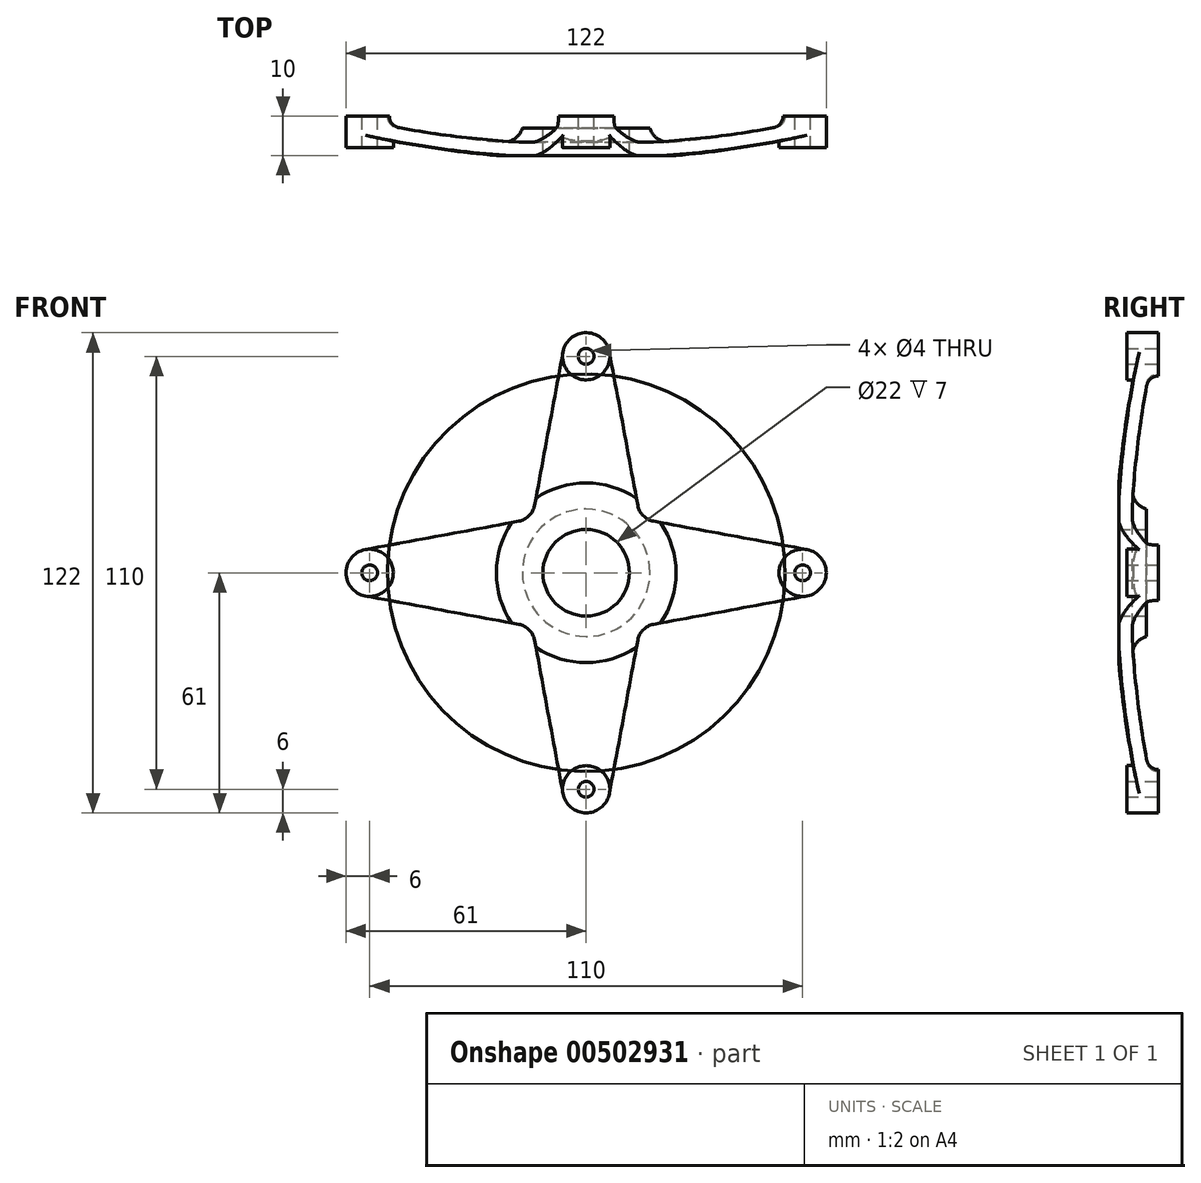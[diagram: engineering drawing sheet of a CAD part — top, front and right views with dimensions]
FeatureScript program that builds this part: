
annotation { "Feature Type Name" : "Feature", "Feature Type Description" : "" }
export const myFeature = defineFeature(function(context is Context, id is Id, definition is map)
    precondition{}
    {
        {
            var Q0;
            Q0=qCreatedBy(makeId("Front.planeOp"),FACE);
            var sketch = newSketch(context, id + "F0", { "sketchPlane" : qUnion([Q0])});
            skCircle(sketch, "E0", {"center": v(0, 55) * mm, "radius": 2 * mm});
            skCircle(sketch, "E1", {"center": v(0, 0) * mm, "radius": 16 * mm});
            skCircle(sketch, "E2", {"center": v(0, 0) * mm, "radius": 11 * mm});
            skCircle(sketch, "E3", {"center": v(0, 55) * mm, "radius": 6 * mm});
            skLineSegment(sketch, "E4", {"start": v(-13.1, 17.11) * mm, "end": v(-5.9, 56.1) * mm});
            skLineSegment(sketch, "E5", {"start": v(13.1, 17.11) * mm, "end": v(5.9, 56.1) * mm});
            skCircle(sketch, "E6.1.0", {"center": v(-55, 0) * mm, "radius": 2 * mm});
            skCircle(sketch, "E6.1.1", {"center": v(-55, 0) * mm, "radius": 6 * mm});
            skLineSegment(sketch, "E6.1.2", {"start": v(-17.11, 13.1) * mm, "end": v(-56.1, 5.9) * mm});
            skLineSegment(sketch, "E6.1.3", {"start": v(-17.11, -13.1) * mm, "end": v(-56.1, -5.9) * mm});
            skCircle(sketch, "E6.2.0", {"center": v(0, -55) * mm, "radius": 2 * mm});
            skCircle(sketch, "E6.2.1", {"center": v(0, -55) * mm, "radius": 6 * mm});
            skLineSegment(sketch, "E6.2.2", {"start": v(-13.1, -17.11) * mm, "end": v(-5.9, -56.1) * mm});
            skLineSegment(sketch, "E6.2.3", {"start": v(13.1, -17.11) * mm, "end": v(5.9, -56.1) * mm});
            skCircle(sketch, "E6.3.0", {"center": v(55, 0) * mm, "radius": 2 * mm});
            skCircle(sketch, "E6.3.1", {"center": v(55, 0) * mm, "radius": 6 * mm});
            skLineSegment(sketch, "E6.3.2", {"start": v(17.11, -13.1) * mm, "end": v(56.1, -5.9) * mm});
            skLineSegment(sketch, "E6.3.3", {"start": v(17.11, 13.1) * mm, "end": v(56.1, 5.9) * mm});
            skPoint(sketch, "E7.orphan", {"position": v(-15.73, 2.9) * mm});
            skPoint(sketch, "E8.orphan", {"position": v(-2.9, 15.73) * mm});
            skPoint(sketch, "E9.orphan", {"position": v(2.9, 15.73) * mm});
            skPoint(sketch, "E10.orphan", {"position": v(15.73, 2.9) * mm});
            skPoint(sketch, "E11.orphan", {"position": v(15.73, -2.9) * mm});
            skPoint(sketch, "E12.orphan", {"position": v(2.9, -15.73) * mm});
            skPoint(sketch, "E13.orphan", {"position": v(-15.73, -2.9) * mm});
            skPoint(sketch, "E14.orphan", {"position": v(-2.9, -15.73) * mm});
            skPoint(sketch, "E15.visualSharp", {"position": v(-13.73, 13.73) * mm});
            skArc(sketch, "E15.filletArc", {"start": v(-17.11, 13.1) * mm, "mid": v(-14.49, 14.49) * mm, "end": v(-13.1, 17.11) * mm});
            skPoint(sketch, "E16.visualSharp", {"position": v(13.73, 13.73) * mm});
            skArc(sketch, "E16.filletArc", {"start": v(13.1, 17.11) * mm, "mid": v(14.49, 14.49) * mm, "end": v(17.11, 13.1) * mm});
            skPoint(sketch, "E17.visualSharp", {"position": v(13.73, -13.73) * mm});
            skArc(sketch, "E17.filletArc", {"start": v(17.11, -13.1) * mm, "mid": v(14.49, -14.49) * mm, "end": v(13.1, -17.11) * mm});
            skPoint(sketch, "E18.visualSharp", {"position": v(-13.73, -13.73) * mm});
            skArc(sketch, "E18.filletArc", {"start": v(-13.1, -17.11) * mm, "mid": v(-14.49, -14.49) * mm, "end": v(-17.11, -13.1) * mm});
            skSolve(sketch);
        }
        {
            var Q0;
            Q0=makeQuery(id+"F0.imprint","IMPRINT",FACE,{"disambiguationData":[TD([[makeQuery(id+"F0.imprint","IMPRINT",EDGE,{"derivedFrom":sQuery(id+"F0.wireOp",EDGE,"E1")}),1.0]])]});
            var Q1;
            Q1=makeQuery(id+"F0.imprint","IMPRINT",FACE,{"disambiguationData":[TD([[makeQuery(id+"F0.imprint","IMPRINT",EDGE,{"derivedFrom":sQuery(id+"F0.wireOp",EDGE,"E1")}),-1.0]])]});
            var Q2;
            Q2=makeQuery(id+"F0.imprint","IMPRINT",FACE,{"disambiguationData":[TD([[makeQuery(id+"F0.imprint","IMPRINT",EDGE,{"derivedFrom":sQuery(id+"F0.wireOp",EDGE,"E6.1.0")}),-1.0]])]});
            var Q3;
            Q3=makeQuery(id+"F0.imprint","IMPRINT",FACE,{"disambiguationData":[TD([[makeQuery(id+"F0.imprint","IMPRINT",EDGE,{"derivedFrom":sQuery(id+"F0.wireOp",EDGE,"E6.2.0")}),-1.0]])]});
            var Q4;
            Q4=makeQuery(id+"F0.imprint","IMPRINT",FACE,{"disambiguationData":[TD([[makeQuery(id+"F0.imprint","IMPRINT",EDGE,{"derivedFrom":sQuery(id+"F0.wireOp",EDGE,"E6.3.0")}),-1.0]])]});
            var Q5;
            Q5=makeQuery(id+"F0.imprint","IMPRINT",FACE,{"disambiguationData":[TD([[makeQuery(id+"F0.imprint","IMPRINT",EDGE,{"derivedFrom":sQuery(id+"F0.wireOp",EDGE,"E0")}),-1.0]])]});
            extrude(context, id + "F1", {"entities" : qUnion([Q0, Q1, Q2, Q3, Q4, Q5]), "depth" : 10 * mm});
        }
        {
            var Q0;
            Q0=qCreatedBy(makeId("Right.planeOp"),FACE);
            var sketch = newSketch(context, id + "F2", { "sketchPlane" : qUnion([Q0])});
            skLineSegment(sketch, "E19", {"start": v(0, 50.5) * mm, "end": v(0, 50.5) * mm});
            skLineSegment(sketch, "E20", {"start": v(-3, 47.5) * mm, "end": v(-3, 11) * mm});
            skLineSegment(sketch, "E21", {"start": v(-3, 11) * mm, "end": v(0, 11) * mm});
            skLineSegment(sketch, "E22", {"start": v(0, 11) * mm, "end": v(0, 50.5) * mm});
            skPoint(sketch, "E23.visualSharp", {"position": v(-3, 50.5) * mm});
            skArc(sketch, "E23.filletArc", {"start": v(0, 50.5) * mm, "mid": v(-2.12, 49.62) * mm, "end": v(-3, 47.5) * mm});
            skArc(sketch, "E24", {"start": v(-2.78, 65) * mm, "mid": v(-8.61, 35.24) * mm, "end": v(-10.95, 5) * mm});
            skLineSegment(sketch, "E25", {"start": v(-10.95, 5) * mm, "end": v(-20, 5) * mm});
            skLineSegment(sketch, "E26", {"start": v(-20, 5) * mm, "end": v(-20, 65) * mm});
            skLineSegment(sketch, "E27", {"start": v(-20, 65) * mm, "end": v(-2.78, 65) * mm});
            skArc(sketch, "E28", {"start": v(-2.95, 48.06) * mm, "mid": v(-5.11, 34.79) * mm, "end": v(-6.58, 21.42) * mm});
            skLineSegment(sketch, "E29", {"start": v(0, 16) * mm, "end": v(-1.6, 16) * mm});
            skPoint(sketch, "E30.visualSharp", {"position": v(-6.97, 16) * mm});
            skArc(sketch, "E30.filletArc", {"start": v(-6.58, 21.42) * mm, "mid": v(-5.28, 17.61) * mm, "end": v(-1.6, 16) * mm});
            skSolve(sketch);
        }
        {
            var Q0;
            Q0=makeQuery(id+"F2.imprint","IMPRINT",FACE,{"disambiguationData":[TD([[makeQuery(id+"F2.imprint","IMPRINT",EDGE,{"derivedFrom":sQuery(id+"F2.wireOp",EDGE,"E24")}),-1.0]])]});
            var Q1;
            Q1=makeQuery(id+"F1.opExtrude","CAP_EDGE",EDGE,{"disambiguationData":[OSD([sQuery(id+"F0.wireOp",EDGE,"E2")])],"isStart":false});
            revolve(context, id + "F3", {"operationType" : NewBodyOperationType.REMOVE, "entities" : qUnion([Q0]), "axis" : qUnion([Q1]), "revolveType" : RevolveType.FULL, "oppositeDirection" : true});
        }
        {
            var Q0;
            Q0=makeQuery(id+"F0.imprint","IMPRINT",FACE,{"disambiguationData":[TD([[makeQuery(id+"F0.imprint","IMPRINT",EDGE,{"derivedFrom":sQuery(id+"F0.wireOp",EDGE,"E0")}),-1.0]])]});
            var Q1;
            Q1=makeQuery(id+"F0.imprint","IMPRINT",FACE,{"disambiguationData":[TD([[makeQuery(id+"F0.imprint","IMPRINT",EDGE,{"derivedFrom":sQuery(id+"F0.wireOp",EDGE,"E6.1.0")}),-1.0]])]});
            var Q2;
            Q2=makeQuery(id+"F0.imprint","IMPRINT",FACE,{"disambiguationData":[TD([[makeQuery(id+"F0.imprint","IMPRINT",EDGE,{"derivedFrom":sQuery(id+"F0.wireOp",EDGE,"E6.3.0")}),-1.0]])]});
            var Q3;
            Q3=makeQuery(id+"F0.imprint","IMPRINT",FACE,{"disambiguationData":[TD([[makeQuery(id+"F0.imprint","IMPRINT",EDGE,{"derivedFrom":sQuery(id+"F0.wireOp",EDGE,"E6.2.0")}),-1.0]])]});
            extrude(context, id + "F4", {"entities" : qUnion([Q0, Q1, Q2, Q3]), "operationType" : NewBodyOperationType.ADD, "depth" : 8 * mm});
        }
        {
            var Q0;
            {var subQ5=sQuery(id+"F2.wireOp",EDGE,"E28");Q0=makeQuery(id+"F2.imprint","IMPRINT",FACE,{"disambiguationData":[TD([[makeQuery(id+"F2.imprint","IMPRINT",EDGE,{"derivedFrom":subQ5}),1.0]])]});}
            var Q1;
            {var subQ6=sQuery(id+"F2.wireOp",EDGE,"E29");Q1=makeQuery(id+"F2.imprint","IMPRINT",FACE,{"disambiguationData":[TD([[makeQuery(id+"F2.imprint","IMPRINT",EDGE,{"derivedFrom":subQ6}),-1.0]])]});}
            var Q2;
            {var subQ1=sQuery(id+"F2.wireOp",EDGE,"E21");Q2=makeQuery(id+"F2.imprint","IMPRINT",FACE,{"disambiguationData":[TD([[makeQuery(id+"F2.imprint","IMPRINT",EDGE,{"derivedFrom":subQ1}),1.0]])]});}
            var Q3;
            Q3=makeQuery(id+"F1.opExtrude","CAP_EDGE",EDGE,{"disambiguationData":[OSD([sQuery(id+"F0.wireOp",EDGE,"E2")])],"isStart":false});
            revolve(context, id + "F5", {"operationType" : NewBodyOperationType.REMOVE, "entities" : qUnion([Q0, Q1, Q2]), "axis" : qUnion([Q3]), "revolveType" : RevolveType.FULL, "oppositeDirection" : true});
        }
    });
